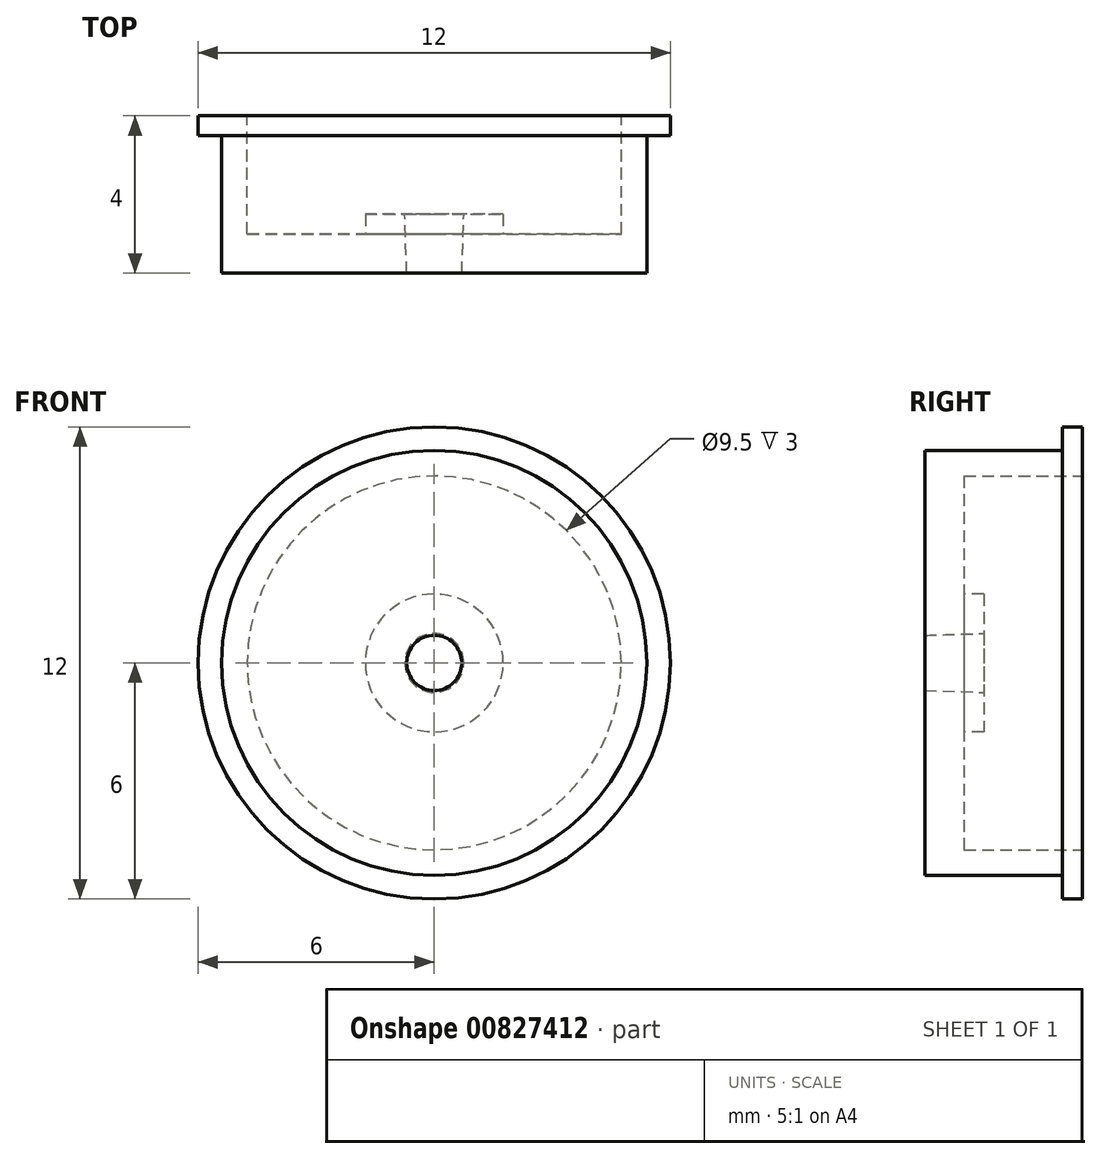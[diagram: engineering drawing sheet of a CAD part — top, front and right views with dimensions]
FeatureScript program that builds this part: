
annotation { "Feature Type Name" : "Feature", "Feature Type Description" : "" }
export const myFeature = defineFeature(function(context is Context, id is Id, definition is map)
    precondition{}
    {
        {
            var Q0;
            Q0=qCreatedBy(makeId("Front.planeOp"),FACE);
            var sketch = newSketch(context, id + "F0", { "sketchPlane" : qUnion([Q0])});
            skCircle(sketch, "E0", {"center": v(0, 0) * mm, "radius": 5.4 * mm});
            skSolve(sketch);
        }
        {
            var Q0;
            Q0=makeQuery(id+"F0.imprint","IMPRINT",FACE,{"disambiguationData":[TD([[makeQuery(id+"F0.imprint","IMPRINT",EDGE,{"derivedFrom":sQuery(id+"F0.wireOp",EDGE,"E0")}),1.0]])]});
            extrude(context, id + "F1", {"entities" : qUnion([Q0]), "depth" : 3.5 * mm, "offsetDistance" : 25 * mm});
        }
        {
            var Q0;
            Q0=makeQuery(id+"F1.opExtrude","CAP_FACE",FACE,{"disambiguationData":[OSD([sQuery(id+"F0.wireOp",EDGE,"E0")])],"isStart":true});
            var sketch = newSketch(context, id + "F2", { "sketchPlane" : qUnion([Q0])});
            skCircle(sketch, "E1", {"center": v(0, 0) * mm, "radius": 6 * mm});
            skSolve(sketch);
        }
        {
            var Q0;
            Q0=makeQuery(id+"F2.imprint","IMPRINT",FACE,{"disambiguationData":[TD([[makeQuery(id+"F2.imprint","IMPRINT",EDGE,{"derivedFrom":sQuery(id+"F2.wireOp",EDGE,"E1")}),1.0]])]});
            var Q1;
            Q1=makeQuery(id+"F2.imprint","IMPRINT",FACE,{"disambiguationData":[TD([[makeQuery(id+"F2.imprint","IMPRINT",EDGE,{"derivedFrom":makeQuery(id+"F1.opExtrude","CAP_EDGE",EDGE,{"disambiguationData":[OSD([sQuery(id+"F0.wireOp",EDGE,"E0")])],"isStart":true})}),-1.0]])]});
            extrude(context, id + "F3", {"entities" : qUnion([Q0, Q1]), "operationType" : NewBodyOperationType.ADD, "depth" : 0.5 * mm, "offsetDistance" : 25 * mm});
        }
        {
            var Q0;
            Q0=makeQuery(id+"F3.opExtrude","CAP_FACE",FACE,{"disambiguationData":[OSD([sQuery(id+"F2.wireOp",EDGE,"E1")])],"isStart":false});
            var sketch = newSketch(context, id + "F4", { "sketchPlane" : qUnion([Q0])});
            skCircle(sketch, "E2", {"center": v(0, 0) * mm, "radius": 4.75 * mm});
            skSolve(sketch);
        }
        {
            var Q0;
            Q0=makeQuery(id+"F4.imprint","IMPRINT",FACE,{"disambiguationData":[TD([[makeQuery(id+"F4.imprint","IMPRINT",EDGE,{"derivedFrom":sQuery(id+"F4.wireOp",EDGE,"E2")}),1.0]])]});
            extrude(context, id + "F5", {"entities" : qUnion([Q0]), "operationType" : NewBodyOperationType.REMOVE, "oppositeDirection" : true, "depth" : 3 * mm, "offsetDistance" : 25 * mm});
        }
        {
            var Q0;
            Q0=makeQuery(id+"F1.opExtrude","CAP_FACE",FACE,{"disambiguationData":[OSD([sQuery(id+"F0.wireOp",EDGE,"E0")])],"isStart":false});
            var sketch = newSketch(context, id + "F6", { "sketchPlane" : qUnion([Q0])});
            skCircle(sketch, "E3", {"center": v(0, 0) * mm, "radius": 0.7 * mm});
            skSolve(sketch);
        }
        {
            var Q0;
            Q0=makeQuery(id+"F5.boolean.opBoolean","COPY",FACE,{"derivedFrom":makeQuery(id+"F5.opExtrude","CAP_FACE",FACE,{"disambiguationData":[OSD([sQuery(id+"F4.wireOp",EDGE,"E2")])],"isStart":false})});
            var sketch = newSketch(context, id + "F7", { "sketchPlane" : qUnion([Q0])});
            skCircle(sketch, "E4", {"center": v(0, 0) * mm, "radius": 1.75 * mm});
            skSolve(sketch);
        }
        {
            var Q0;
            Q0=makeQuery(id+"F7.imprint","IMPRINT",FACE,{"disambiguationData":[TD([[makeQuery(id+"F7.imprint","IMPRINT",EDGE,{"derivedFrom":sQuery(id+"F7.wireOp",EDGE,"E4")}),1.0]])]});
            extrude(context, id + "F8", {"entities" : qUnion([Q0]), "operationType" : NewBodyOperationType.ADD, "depth" : 0.5 * mm, "offsetDistance" : 25 * mm});
        }
        {
            var Q0;
            Q0=makeQuery(id+"F8.opExtrude","CAP_FACE",FACE,{"disambiguationData":[OSD([sQuery(id+"F7.wireOp",EDGE,"E4")])],"isStart":false});
            var sketch = newSketch(context, id + "F9", { "sketchPlane" : qUnion([Q0])});
            skCircle(sketch, "E5", {"center": v(0, 0) * mm, "radius": 0.75 * mm});
            skSolve(sketch);
        }
        {
            var Q1;
            Q1=makeQuery(id+"F9.imprint","IMPRINT",FACE,{"disambiguationData":[TD([[makeQuery(id+"F9.imprint","IMPRINT",EDGE,{"derivedFrom":sQuery(id+"F9.wireOp",EDGE,"E5")}),1.0]])]});
            var Q2;
            Q2=makeQuery(id+"F6.imprint","IMPRINT",FACE,{"disambiguationData":[TD([[makeQuery(id+"F6.imprint","IMPRINT",EDGE,{"derivedFrom":sQuery(id+"F6.wireOp",EDGE,"E3")}),1.0]])]});
            loft(context, id + "F10", {"operationType" : NewBodyOperationType.REMOVE, "sheetProfilesArray" : [{ "sheetProfileEntities" : qUnion([Q1]) }, { "sheetProfileEntities" : qUnion([Q2]) }]});
        }
    });
